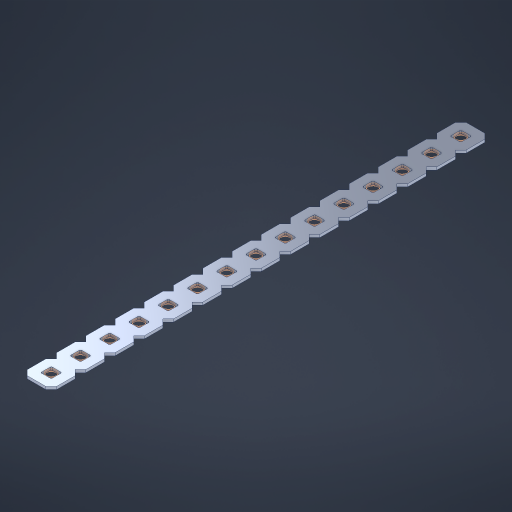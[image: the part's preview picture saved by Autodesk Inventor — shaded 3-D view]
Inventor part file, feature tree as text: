
AUTODESK INVENTOR PART (.ipt)
format: ipt  version: 2023 (Build 270158000, 158)  size: 453,632 bytes
history: native  units: in
note: dims shown in document units (in); Inventor stores cm internally (conversion verified against a paired STEP export)
features: other x16, extrude x14, sketch x2, pattern_linear x1
ambient origin geometry x8: Origin, YZ Plane, XZ Plane, XY Plane, X Axis, Y Axis, Z Axis, Center Point
bodies: Solid1 (feature_tree), Body (feature_tree)
feature tree (33):
  pattern_linear  "Rectangular Pattern1"  Spacing1=0.09in  [1 undecoded]
  sketch  "Sketch1"  dims[d1=0.5in]
  sketch  "Sketch2"  dims[d2=0.182in d3=0.09in d4=0.09in d5=0.09in d6=0.09in d7=0.09in d8=0.09in d9=0.09in d10=0.09in d11=0.02in d13=0.0in d14=0.172in d15=0.0625in d16=0.0in d19=0.5in d22=0.5in]
  other  "Srf1"
  other  "Srf126"
  other  "Srf127"
  other  "Srf128"
  other  "Srf129"
  other  "Srf130"
  other  "Srf131"
  other  "Srf250"
  other  "Srf251"
  other  "Srf252"
  other  "Srf253"
  other  "Srf254"
  other  "Srf255"
  other  "Srf256"
  other  "Srf257"
  other  "Circle"
  extrude  "ExtrusionSrf126"  Depth=0.09in
  extrude  "ExtrusionSrf127"  Depth=0.09in
  extrude  "ExtrusionSrf128"  Depth=0.09in
  extrude  "ExtrusionSrf129"  Depth=0.09in
  extrude  "ExtrusionSrf130"  Depth=0.09in
  extrude  "ExtrusionSrf131"  Depth=0.09in
  extrude  "ExtrusionSrf250"  Depth=0.09in
  extrude  "ExtrusionSrf251"  Depth=0.02in
  extrude  "ExtrusionSrf252"  TaperAngle=0.0deg  [1 undecoded]
  extrude  "ExtrusionSrf253"  Depth=0.5in
  extrude  "ExtrusionSrf254"  Depth=0.5in TaperAngle=0.0deg
  extrude  "ExtrusionSrf255"  Depth=0.5in
  extrude  "ExtrusionSrf256"  Depth=0.5in
  extrude  "ExtrusionSrf257"  [1 undecoded]
note: 3 required parameter values undecoded (feature->parameter linkage not recoverable at this tier; creation-order binding heuristic only, values carry confidence <= 0.55)
